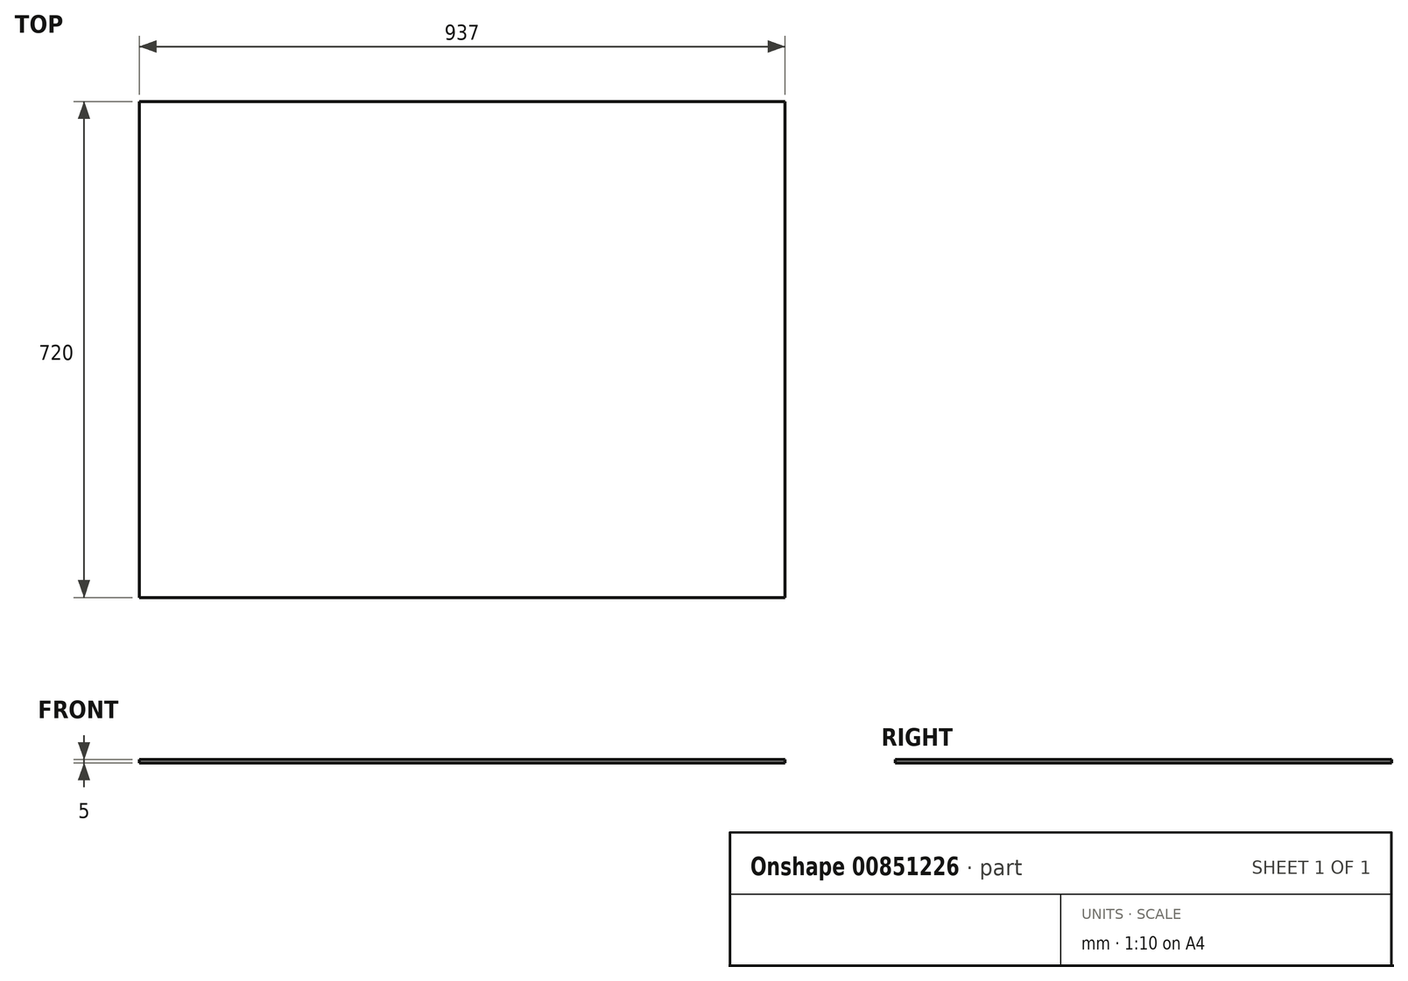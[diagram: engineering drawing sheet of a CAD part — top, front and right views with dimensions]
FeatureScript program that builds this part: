
annotation { "Feature Type Name" : "Feature", "Feature Type Description" : "" }
export const myFeature = defineFeature(function(context is Context, id is Id, definition is map)
    precondition{}
    {
        {
            var Q0;
            Q0=qCreatedBy(makeId("Top.planeOp"),FACE);
            var sketch = newSketch(context, id + "F0", { "sketchPlane" : qUnion([Q0])});
            skLineSegment(sketch, "E0.bottom", {"start": v(-468.5, 360) * mm, "end": v(468.5, 360) * mm});
            skLineSegment(sketch, "E0.top", {"start": v(-468.5, -360) * mm, "end": v(468.5, -360) * mm});
            skLineSegment(sketch, "E0.left", {"start": v(-468.5, 360) * mm, "end": v(-468.5, -360) * mm});
            skLineSegment(sketch, "E0.right", {"start": v(468.5, 360) * mm, "end": v(468.5, -360) * mm});
            skSolve(sketch);
        }
        {
            var Q0;
            Q0=makeQuery(id+"F0.imprint","IMPRINT",FACE,{"disambiguationData":[TD([[makeQuery(id+"F0.imprint","IMPRINT",EDGE,{"derivedFrom":sQuery(id+"F0.wireOp",EDGE,"E0.bottom")}),-1.0]])]});
            extrude(context, id + "F1", {"entities" : qUnion([Q0]), "endBound" : BoundingType.SYMMETRIC, "depth" : 5 * mm, "offsetDistance" : 25 * mm});
        }
    });
